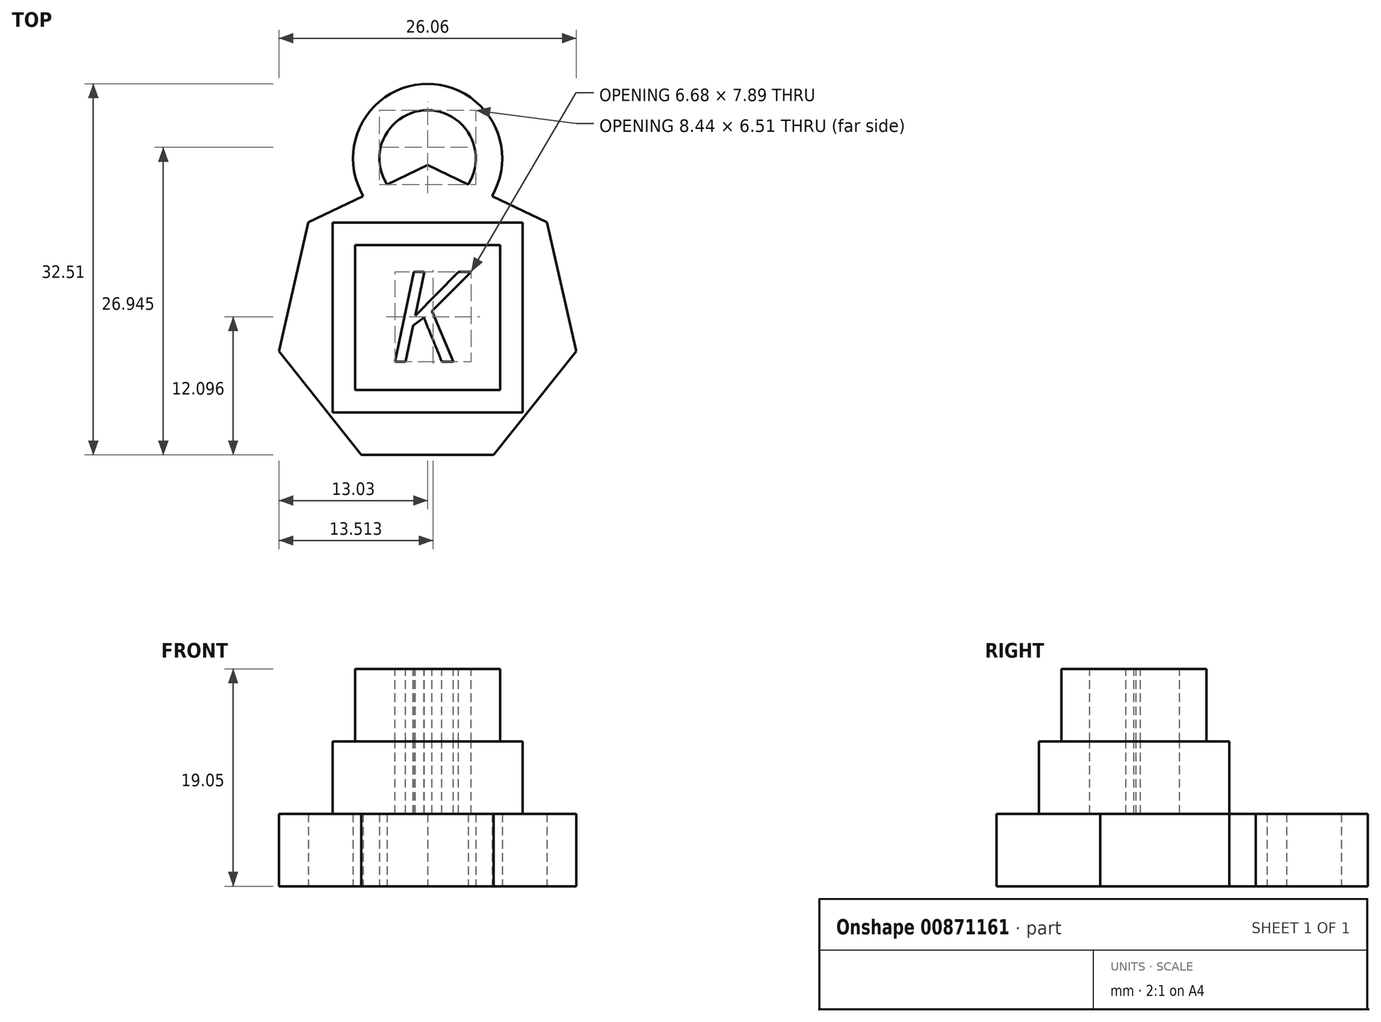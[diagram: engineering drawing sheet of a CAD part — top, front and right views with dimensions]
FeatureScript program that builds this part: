
annotation { "Feature Type Name" : "Feature", "Feature Type Description" : "" }
export const myFeature = defineFeature(function(context is Context, id is Id, definition is map)
    precondition{}
    {
        {
            var Q0;
            Q0=qCreatedBy(makeId("Top.planeOp"),FACE);
            var sketch = newSketch(context, id + "F0", { "sketchPlane" : qUnion([Q0])});
            skCircle(sketch, "E0.cCircle", {"center": v(0, 0) * mm, "radius": 12.04 * mm, "construction": true});
            skLineSegment(sketch, "E0.0", {"start": v(13.03, -2.97) * mm, "end": v(5.8, -12.04) * mm});
            skLineSegment(sketch, "E0.1", {"start": v(5.8, -12.04) * mm, "end": v(-5.8, -12.04) * mm});
            skLineSegment(sketch, "E0.2", {"start": v(-5.8, -12.04) * mm, "end": v(-13.03, -2.97) * mm});
            skLineSegment(sketch, "E0.3", {"start": v(-13.03, -2.97) * mm, "end": v(-10.45, 8.33) * mm});
            skLineSegment(sketch, "E0.4", {"start": v(-10.45, 8.33) * mm, "end": v(0, 13.36) * mm});
            skLineSegment(sketch, "E0.5", {"start": v(0, 13.36) * mm, "end": v(10.45, 8.33) * mm});
            skLineSegment(sketch, "E0.6", {"start": v(10.45, 8.33) * mm, "end": v(13.03, -2.97) * mm});
            skPoint(sketch, "E0.0.midPoint", {"position": v(9.41, -7.5) * mm});
            skSolve(sketch);
        }
        {
            var Q0;
            Q0=makeQuery(id+"F0.imprint","IMPRINT",FACE,{"disambiguationData":[TD([[makeQuery(id+"F0.imprint","IMPRINT",EDGE,{"derivedFrom":sQuery(id+"F0.wireOp",EDGE,"E0.0")}),-1.0]])]});
            extrude(context, id + "F1", {"entities" : qUnion([Q0]), "depth" : 6.35 * mm, "offsetDistance" : 25.4 * mm});
        }
        {
            var Q0;
            Q0=makeQuery(id+"F1.opExtrude","CAP_FACE",FACE,{"disambiguationData":[OSD([sQuery(id+"F0.wireOp",EDGE,"E0.0"),sQuery(id+"F0.wireOp",EDGE,"E0.1"),sQuery(id+"F0.wireOp",EDGE,"E0.2"),sQuery(id+"F0.wireOp",EDGE,"E0.3"),sQuery(id+"F0.wireOp",EDGE,"E0.4"),sQuery(id+"F0.wireOp",EDGE,"E0.5"),sQuery(id+"F0.wireOp",EDGE,"E0.6")])],"isStart":false});
            var sketch = newSketch(context, id + "F2", { "sketchPlane" : qUnion([Q0])});
            skCircle(sketch, "E1.cCircle", {"center": v(0, 0) * mm, "radius": 8.33 * mm, "construction": true});
            skPoint(sketch, "E1.0.midPoint", {"position": v(0, -8.33) * mm});
            skLineSegment(sketch, "E2.0", {"start": v(-8.33, 8.33) * mm, "end": v(8.33, 8.33) * mm});
            skLineSegment(sketch, "E2.1", {"start": v(8.33, 8.33) * mm, "end": v(8.33, -8.33) * mm});
            skLineSegment(sketch, "E2.2", {"start": v(8.33, -8.33) * mm, "end": v(-8.33, -8.33) * mm});
            skLineSegment(sketch, "E2.3", {"start": v(-8.33, -8.33) * mm, "end": v(-8.33, 8.33) * mm});
            skPoint(sketch, "E2.0.midPoint", {"position": v(0, 8.33) * mm});
            skSolve(sketch);
        }
        {
            var Q0;
            Q0=makeQuery(id+"F2.imprint","IMPRINT",FACE,{"disambiguationData":[TD([[makeQuery(id+"F2.imprint","IMPRINT",EDGE,{"derivedFrom":sQuery(id+"F2.wireOp",EDGE,"E2.0")}),-1.0]])]});
            extrude(context, id + "F3", {"entities" : qUnion([Q0]), "operationType" : NewBodyOperationType.ADD, "depth" : 6.35 * mm, "offsetDistance" : 25.4 * mm});
        }
        {
            var Q0;
            Q0=makeQuery(id+"F3.opExtrude","CAP_FACE",FACE,{"disambiguationData":[OSD([sQuery(id+"F2.wireOp",EDGE,"E2.0"),sQuery(id+"F2.wireOp",EDGE,"E2.1"),sQuery(id+"F2.wireOp",EDGE,"E2.2"),sQuery(id+"F2.wireOp",EDGE,"E2.3")])],"isStart":false});
            var sketch = newSketch(context, id + "F4", { "sketchPlane" : qUnion([Q0])});
            skCircle(sketch, "E3.cCircle", {"center": v(0, 0) * mm, "radius": 6.35 * mm, "construction": true});
            skLineSegment(sketch, "E3.0", {"start": v(6.35, 6.35) * mm, "end": v(6.35, -6.35) * mm});
            skLineSegment(sketch, "E3.1", {"start": v(6.35, -6.35) * mm, "end": v(-6.35, -6.35) * mm});
            skLineSegment(sketch, "E3.2", {"start": v(-6.35, -6.35) * mm, "end": v(-6.35, 6.35) * mm});
            skLineSegment(sketch, "E3.3", {"start": v(-6.35, 6.35) * mm, "end": v(6.35, 6.35) * mm});
            skPoint(sketch, "E3.0.midPoint", {"position": v(6.35, 0) * mm});
            skSolve(sketch);
        }
        {
            var Q0;
            Q0=makeQuery(id+"F4.imprint","IMPRINT",FACE,{"disambiguationData":[TD([[makeQuery(id+"F4.imprint","IMPRINT",EDGE,{"derivedFrom":sQuery(id+"F4.wireOp",EDGE,"E3.0")}),-1.0]])]});
            extrude(context, id + "F5", {"entities" : qUnion([Q0]), "depth" : 6.35 * mm, "offsetDistance" : 25.4 * mm});
        }
        {
            var Q0;
            Q0=makeQuery(id+"F5.opExtrude","CAP_FACE",FACE,{"disambiguationData":[OSD([sQuery(id+"F4.wireOp",EDGE,"E3.0"),sQuery(id+"F4.wireOp",EDGE,"E3.1"),sQuery(id+"F4.wireOp",EDGE,"E3.2"),sQuery(id+"F4.wireOp",EDGE,"E3.3")])],"isStart":false});
            var sketch = newSketch(context, id + "F6", { "sketchPlane" : qUnion([Q0])});
            skText(sketch, "E4", { "text": "K", "fontName": "OpenSans-Italic.ttf"});
            const initialGuessF6  = {"E4": [-0.00332, -0.00389, 1, 0, 0.00796]};
            skSetInitialGuess(sketch, initialGuessF6);
            skSolve(sketch);
        }
        {
            var Q0;
            Q0 = qSketchRegion(id + "F6", true);
            extrude(context, id + "F7", {"entities" : qUnion([Q0]), "operationType" : NewBodyOperationType.REMOVE, "oppositeDirection" : true, "depth" : 12.7 * mm, "offsetDistance" : 25.4 * mm});
        }
        {
            var Q0;
            Q0 = qSketchRegion(id + "F6", true);
            extrude(context, id + "F8", {"entities" : qUnion([Q0]), "operationType" : NewBodyOperationType.REMOVE, "oppositeDirection" : true, "depth" : 12.7 * mm, "offsetDistance" : 25.4 * mm});
        }
        {
            var Q0;
            Q0=qCreatedBy(makeId("Top.planeOp"),FACE);
            var sketch = newSketch(context, id + "F9", { "sketchPlane" : qUnion([Q0])});
            skCircle(sketch, "E5", {"center": v(0, 13.94) * mm, "radius": 6.53 * mm});
            skCircle(sketch, "E6", {"center": v(0, 13.94) * mm, "radius": 4.22 * mm});
            skSolve(sketch);
        }
        {
            var Q0;
            Q0=makeQuery(id+"F9.imprint","IMPRINT",FACE,{"disambiguationData":[TD([[makeQuery(id+"F9.imprint","IMPRINT",EDGE,{"derivedFrom":sQuery(id+"F9.wireOp",EDGE,"E5")}),1.0]])]});
            extrude(context, id + "F10", {"entities" : qUnion([Q0]), "operationType" : NewBodyOperationType.ADD, "depth" : 6.35 * mm, "offsetDistance" : 25.4 * mm});
        }
    });
